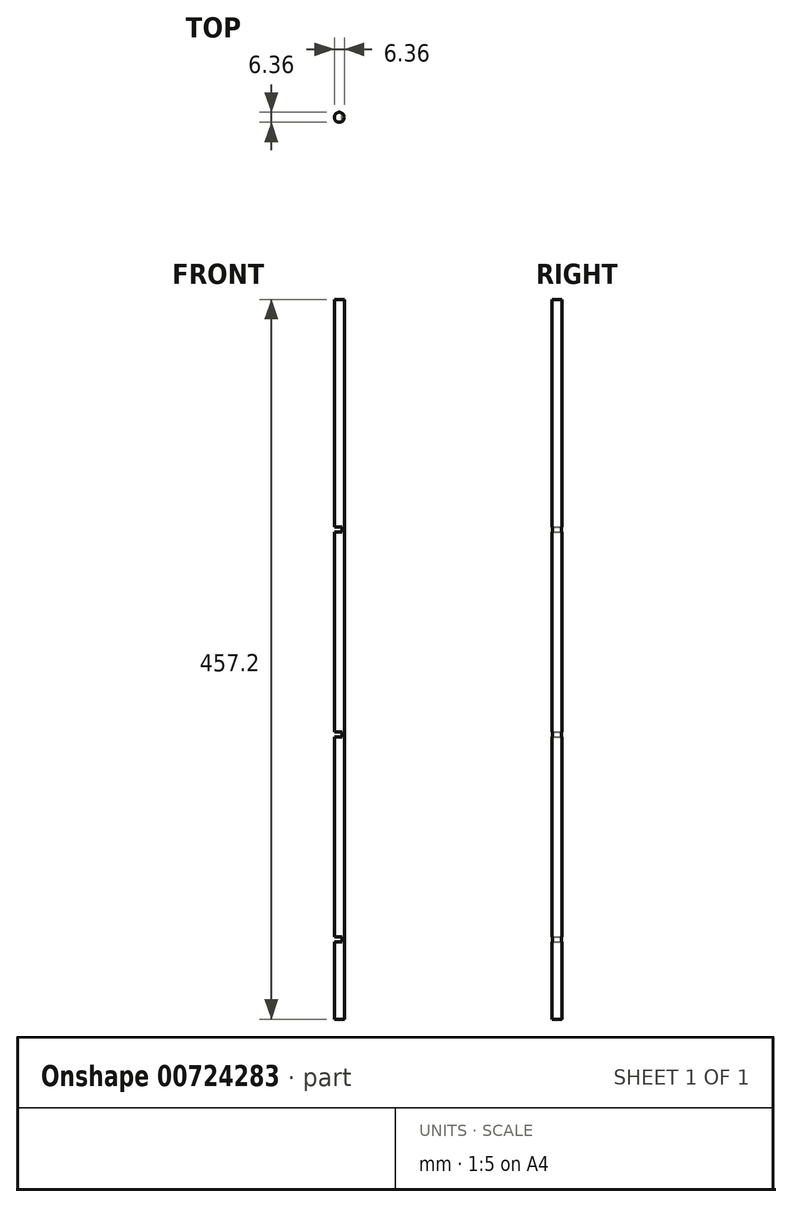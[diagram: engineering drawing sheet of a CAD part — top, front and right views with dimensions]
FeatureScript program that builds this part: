
annotation { "Feature Type Name" : "Feature", "Feature Type Description" : "" }
export const myFeature = defineFeature(function(context is Context, id is Id, definition is map)
    precondition{}
    {
        {
            var Q0;
            Q0=qCreatedBy(makeId("Top.planeOp"),FACE);
            var sketch = newSketch(context, id + "F0", { "sketchPlane" : qUnion([Q0])});
            skCircle(sketch, "E0", {"center": v(0, 0) * mm, "radius": 3.18 * mm});
            skSolve(sketch);
        }
        {
            var Q0;
            Q0 = qSketchRegion(id + "F0", true);
            extrude(context, id + "F1", {"entities" : qUnion([Q0]), "endBound" : BoundingType.SYMMETRIC, "depth" : 457.2 * mm, "offsetDistance" : 25.4 * mm});
        }
        {
            var Q0;
            Q0=qCreatedBy(makeId("Front.planeOp"),FACE);
            var sketch = newSketch(context, id + "F2", { "sketchPlane" : qUnion([Q0])});
            skLineSegment(sketch, "E1.bottom", {"start": v(1.59, -176.2) * mm, "end": v(-49.21, -176.2) * mm});
            skLineSegment(sketch, "E1.top", {"start": v(1.59, -179.4) * mm, "end": v(-49.21, -179.4) * mm});
            skLineSegment(sketch, "E1.left", {"start": v(1.59, -176.2) * mm, "end": v(1.59, -179.4) * mm});
            skLineSegment(sketch, "E1.right", {"start": v(-49.21, -176.2) * mm, "end": v(-49.21, -179.4) * mm});
            skPoint(sketch, "E1.middle", {"position": v(-23.81, -177.8) * mm});
            skPoint(sketch, "E2", {"position": v(0, -228.6) * mm});
            skLineSegment(sketch, "E3", {"start": v(-3.18, -228.6) * mm, "end": v(3.18, -228.6) * mm});
            skPoint(sketch, "E4", {"position": v(0, 0) * mm});
            skLineSegment(sketch, "E5.bottom", {"start": v(1.59, -46) * mm, "end": v(-49.21, -46) * mm});
            skLineSegment(sketch, "E5.top", {"start": v(1.59, -49.2) * mm, "end": v(-49.21, -49.2) * mm});
            skLineSegment(sketch, "E5.left", {"start": v(1.59, -46) * mm, "end": v(1.59, -49.2) * mm});
            skLineSegment(sketch, "E5.right", {"start": v(-49.21, -46) * mm, "end": v(-49.21, -49.2) * mm});
            skPoint(sketch, "E5.middle", {"position": v(-23.81, -47.6) * mm});
            skLineSegment(sketch, "E6.bottom", {"start": v(1.59, 84.2) * mm, "end": v(-49.21, 84.2) * mm});
            skLineSegment(sketch, "E6.top", {"start": v(1.59, 81) * mm, "end": v(-49.21, 81) * mm});
            skLineSegment(sketch, "E6.left", {"start": v(1.59, 84.2) * mm, "end": v(1.59, 81) * mm});
            skLineSegment(sketch, "E6.right", {"start": v(-49.21, 84.2) * mm, "end": v(-49.21, 81) * mm});
            skPoint(sketch, "E6.middle", {"position": v(-23.81, 82.6) * mm});
            skSolve(sketch);
        }
        {
            var Q0;
            Q0 = qSketchRegion(id + "F2", true);
            extrude(context, id + "F3", {"entities" : qUnion([Q0]), "operationType" : NewBodyOperationType.REMOVE, "endBound" : BoundingType.SYMMETRIC, "depth" : 25.4 * mm, "offsetDistance" : 25.4 * mm});
        }
    });
